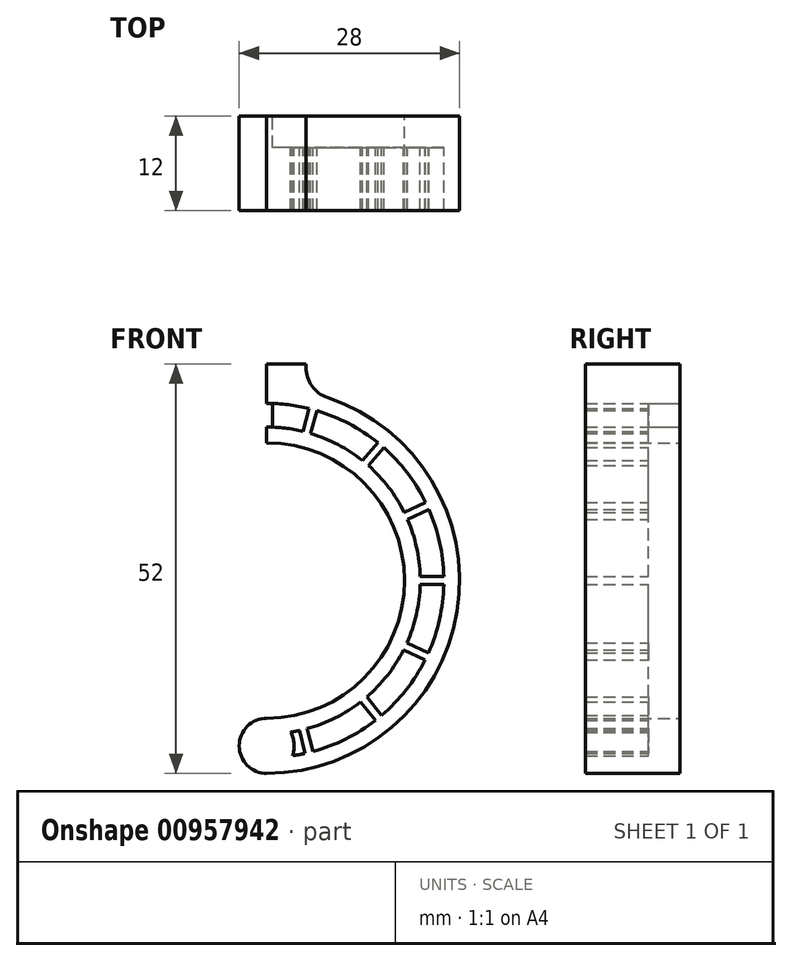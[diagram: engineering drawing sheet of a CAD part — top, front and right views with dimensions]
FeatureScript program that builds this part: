
annotation { "Feature Type Name" : "Feature", "Feature Type Description" : "" }
export const myFeature = defineFeature(function(context is Context, id is Id, definition is map)
    precondition{}
    {
        {
            var Q0;
            Q0=qCreatedBy(makeId("Front.planeOp"),FACE);
            var sketch = newSketch(context, id + "F0", { "sketchPlane" : qUnion([Q0])});
            skArc(sketch, "E0", {"start": v(0, -24.5) * mm, "mid": v(24.18, -3.92) * mm, "end": v(7.73, 23.25) * mm});
            skArc(sketch, "E1", {"start": v(0, -17.5) * mm, "mid": v(17.5, 0) * mm, "end": v(0, 17.5) * mm});
            skArc(sketch, "E2.0", {"start": v(3.04, -19.26) * mm, "mid": v(19.44, 1.52) * mm, "end": v(0, 19.5) * mm});
            skArc(sketch, "E3.0", {"start": v(3.26, -22.26) * mm, "mid": v(22.44, 1.64) * mm, "end": v(0, 22.5) * mm});
            skLineSegment(sketch, "E4", {"start": v(0, 0) * mm, "end": v(0, 29.22) * mm});
            skLineSegment(sketch, "E5", {"start": v(0, 29.22) * mm, "end": v(0, 0) * mm});
            skLineSegment(sketch, "E6", {"start": v(0, -27.59) * mm, "end": v(0, -24.5) * mm});
            skLineSegment(sketch, "E7.top", {"start": v(0, 27.5) * mm, "end": v(5, 27.5) * mm});
            skLineSegment(sketch, "E7.left", {"start": v(0, 17.5) * mm, "end": v(0, 27.5) * mm});
            skLineSegment(sketch, "E8.trimOffspring", {"start": v(5, 27.08) * mm, "end": v(5, 27.5) * mm});
            skCircle(sketch, "E9", {"center": v(0, -21) * mm, "radius": 3.5 * mm});
            skPoint(sketch, "E9.third.point", {"position": v(-3.48, -21.36) * mm});
            skLineSegment(sketch, "E10.trimOffspring", {"start": v(0, -17.5) * mm, "end": v(0, 0) * mm});
            skLineSegment(sketch, "E11.bottom", {"start": v(17.5, -0.5) * mm, "end": v(24.48, -0.5) * mm});
            skLineSegment(sketch, "E11.top", {"start": v(17.5, 0.5) * mm, "end": v(24.48, 0.5) * mm});
            skLineSegment(sketch, "E11.left", {"start": v(17.5, -0.5) * mm, "end": v(17.5, 0.5) * mm});
            skLineSegment(sketch, "E11.right", {"start": v(24.48, -0.5) * mm, "end": v(24.48, 0.5) * mm});
            skPoint(sketch, "E11.middle", {"position": v(20.99, 0) * mm});
            skLineSegment(sketch, "E12.1.0", {"start": v(15.59, -7.95) * mm, "end": v(16.02, -7.05) * mm});
            skLineSegment(sketch, "E12.1.1", {"start": v(21.9, -10.95) * mm, "end": v(22.33, -10.05) * mm});
            skLineSegment(sketch, "E12.1.2", {"start": v(15.59, -7.95) * mm, "end": v(21.9, -10.95) * mm});
            skLineSegment(sketch, "E12.1.3", {"start": v(16.02, -7.05) * mm, "end": v(22.33, -10.05) * mm});
            skLineSegment(sketch, "E12.2.0", {"start": v(10.67, -13.87) * mm, "end": v(11.45, -13.24) * mm});
            skLineSegment(sketch, "E12.2.1", {"start": v(15.1, -19.29) * mm, "end": v(15.87, -18.65) * mm});
            skLineSegment(sketch, "E12.2.2", {"start": v(10.67, -13.87) * mm, "end": v(15.1, -19.29) * mm});
            skLineSegment(sketch, "E12.2.3", {"start": v(11.45, -13.24) * mm, "end": v(15.87, -18.65) * mm});
            skLineSegment(sketch, "E12.3.0", {"start": v(3.7, -17.1) * mm, "end": v(4.66, -16.87) * mm});
            skLineSegment(sketch, "E12.3.1", {"start": v(5.36, -23.9) * mm, "end": v(6.33, -23.65) * mm});
            skLineSegment(sketch, "E12.3.2", {"start": v(3.7, -17.1) * mm, "end": v(5.36, -23.9) * mm});
            skLineSegment(sketch, "E12.3.3", {"start": v(4.66, -16.87) * mm, "end": v(6.33, -23.65) * mm});
            skLineSegment(sketch, "E12.anchor1", {"start": v(0, 0) * mm, "end": v(17.5, -0.5) * mm, "construction": true});
            skLineSegment(sketch, "E12.anchor2", {"start": v(0, 0) * mm, "end": v(3.7, -17.1) * mm, "construction": true});
            skLineSegment(sketch, "E13.1.0", {"start": v(16.07, 6.92) * mm, "end": v(15.65, 7.83) * mm});
            skLineSegment(sketch, "E13.1.1", {"start": v(22.4, 9.87) * mm, "end": v(21.99, 10.78) * mm});
            skLineSegment(sketch, "E13.1.2", {"start": v(16.07, 6.92) * mm, "end": v(22.4, 9.87) * mm});
            skLineSegment(sketch, "E13.1.3", {"start": v(15.65, 7.83) * mm, "end": v(21.99, 10.78) * mm});
            skLineSegment(sketch, "E13.2.0", {"start": v(11.65, 13.06) * mm, "end": v(10.89, 13.7) * mm});
            skLineSegment(sketch, "E13.2.1", {"start": v(16.15, 18.4) * mm, "end": v(15.4, 19.05) * mm});
            skLineSegment(sketch, "E13.2.2", {"start": v(11.65, 13.06) * mm, "end": v(16.15, 18.4) * mm});
            skLineSegment(sketch, "E13.2.3", {"start": v(10.89, 13.7) * mm, "end": v(15.4, 19.05) * mm});
            skLineSegment(sketch, "E13.anchor1", {"start": v(0, 0) * mm, "end": v(17.5, 0.5) * mm, "construction": true});
            skLineSegment(sketch, "E13.anchor2", {"start": v(0, 0) * mm, "end": v(4.1, 17.01) * mm, "construction": true});
            skLineSegment(sketch, "E14.2.3.0", {"start": v(5.06, 16.75) * mm, "end": v(4.1, 17.01) * mm});
            skLineSegment(sketch, "E14.6.3.0", {"start": v(5.06, 16.75) * mm, "end": v(6.37, 21.58) * mm});
            skLineSegment(sketch, "E14.9.3.0", {"start": v(4.1, 17.01) * mm, "end": v(5.4, 21.84) * mm});
            skArc(sketch, "E15.filletArc", {"start": v(5, 27.08) * mm, "mid": v(5.74, 24.72) * mm, "end": v(7.73, 23.25) * mm});
            skLineSegment(sketch, "E16.left", {"start": v(0, 22.5) * mm, "end": v(0, 19.5) * mm});
            skLineSegment(sketch, "E16.right", {"start": v(0.74, 22.49) * mm, "end": v(0.74, 19.49) * mm});
            skSolve(sketch);
        }
        {
            var Q0;
            {var subQ12=sQuery(id+"F0.wireOp",EDGE,"E0");Q0=makeQuery(id+"F0.imprint","IMPRINT",FACE,{"disambiguationData":[TD([[makeQuery(id+"F0.imprint","IMPRINT",EDGE,{"derivedFrom":subQ12}),1.0]])]});}
            var Q1;
            {var subQ5=sQuery(id+"F0.wireOp",EDGE,"E13.2.1");Q1=makeQuery(id+"F0.imprint","IMPRINT",FACE,{"disambiguationData":[TD([[makeQuery(id+"F0.imprint","IMPRINT",EDGE,{"derivedFrom":subQ5}),1.0]])]});}
            var Q2;
            {var subQ5=sQuery(id+"F0.wireOp",EDGE,"E13.1.1");Q2=makeQuery(id+"F0.imprint","IMPRINT",FACE,{"disambiguationData":[TD([[makeQuery(id+"F0.imprint","IMPRINT",EDGE,{"derivedFrom":subQ5}),1.0]])]});}
            var Q3;
            {var subQ5=sQuery(id+"F0.wireOp",EDGE,"E11.right");Q3=makeQuery(id+"F0.imprint","IMPRINT",FACE,{"disambiguationData":[TD([[makeQuery(id+"F0.imprint","IMPRINT",EDGE,{"derivedFrom":subQ5}),1.0]])]});}
            var Q4;
            {var subQ5=sQuery(id+"F0.wireOp",EDGE,"E12.1.1");Q4=makeQuery(id+"F0.imprint","IMPRINT",FACE,{"disambiguationData":[TD([[makeQuery(id+"F0.imprint","IMPRINT",EDGE,{"derivedFrom":subQ5}),1.0]])]});}
            var Q5;
            {var subQ5=sQuery(id+"F0.wireOp",EDGE,"E12.2.1");Q5=makeQuery(id+"F0.imprint","IMPRINT",FACE,{"disambiguationData":[TD([[makeQuery(id+"F0.imprint","IMPRINT",EDGE,{"derivedFrom":subQ5}),1.0]])]});}
            var Q6;
            {var subQ5=sQuery(id+"F0.wireOp",EDGE,"E12.3.1");Q6=makeQuery(id+"F0.imprint","IMPRINT",FACE,{"disambiguationData":[TD([[makeQuery(id+"F0.imprint","IMPRINT",EDGE,{"derivedFrom":subQ5}),1.0]])]});}
            var Q7;
            {var subQ3=sQuery(id+"F0.wireOp",EDGE,"E12.3.3");var subQ5=sQuery(id+"F0.wireOp",EDGE,"E2.0");var subQ6=makeQuery(id+"F0.imprint","INTERSECT",VERTEX,{"derivedFrom":[subQ5,subQ3]});Q7=makeQuery(id+"F0.imprint","IMPRINT",FACE,{"disambiguationData":[TD([[makeQuery(id+"F0.imprint","IMPRINT",EDGE,{"disambiguationData":[TD([[subQ6,-1.0]])],"derivedFrom":subQ5}),1.0]])]});}
            var Q8;
            {var subQ0=sQuery(id+"F0.wireOp",EDGE,"E12.3.2");var subQ6=sQuery(id+"F0.wireOp",EDGE,"E2.0");var subQ7=makeQuery(id+"F0.imprint","INTERSECT",VERTEX,{"derivedFrom":[subQ6,subQ0]});Q8=makeQuery(id+"F0.imprint","IMPRINT",FACE,{"disambiguationData":[TD([[makeQuery(id+"F0.imprint","IMPRINT",EDGE,{"disambiguationData":[TD([[subQ7,-1.0]])],"derivedFrom":subQ6}),1.0]])]});}
            var Q9;
            {var subQ0=sQuery(id+"F0.wireOp",EDGE,"E9");var subQ5=sQuery(id+"F0.wireOp",EDGE,"E2.0");var subQ6=makeQuery(id+"F0.imprint","INTERSECT",VERTEX,{"derivedFrom":[subQ5,subQ0]});Q9=makeQuery(id+"F0.imprint","IMPRINT",FACE,{"disambiguationData":[TD([[makeQuery(id+"F0.imprint","IMPRINT",EDGE,{"disambiguationData":[TD([[subQ6,-1.0]])],"derivedFrom":subQ5}),1.0]])]});}
            var Q10;
            {var subQ0=sQuery(id+"F0.wireOp",EDGE,"E9");var subQ3=makeQuery(id+"F0.imprint","INTERSECT",VERTEX,{"derivedFrom":[sQuery(id+"F0.wireOp",EDGE,"E0"),subQ0]});Q10=makeQuery(id+"F0.imprint","IMPRINT",FACE,{"disambiguationData":[TD([[makeQuery(id+"F0.imprint","IMPRINT",EDGE,{"disambiguationData":[TD([[subQ3,-1.0]])],"derivedFrom":subQ0}),1.0]])]});}
            var Q11;
            {var subQ0=sQuery(id+"F0.wireOp",EDGE,"E12.2.2");var subQ6=sQuery(id+"F0.wireOp",EDGE,"E2.0");var subQ7=makeQuery(id+"F0.imprint","INTERSECT",VERTEX,{"derivedFrom":[subQ6,subQ0]});Q11=makeQuery(id+"F0.imprint","IMPRINT",FACE,{"disambiguationData":[TD([[makeQuery(id+"F0.imprint","IMPRINT",EDGE,{"disambiguationData":[TD([[subQ7,-1.0]])],"derivedFrom":subQ6}),1.0]])]});}
            var Q12;
            {var subQ0=sQuery(id+"F0.wireOp",EDGE,"E12.3.2");var subQ1=sQuery(id+"F0.wireOp",EDGE,"E2.0");var subQ2=makeQuery(id+"F0.imprint","INTERSECT",VERTEX,{"derivedFrom":[subQ1,subQ0]});Q12=makeQuery(id+"F0.imprint","IMPRINT",FACE,{"disambiguationData":[TD([[makeQuery(id+"F0.imprint","IMPRINT",EDGE,{"disambiguationData":[TD([[subQ2,-1.0]])],"derivedFrom":subQ1}),-1.0]])]});}
            var Q13;
            {var subQ0=sQuery(id+"F0.wireOp",EDGE,"E12.2.2");var subQ1=sQuery(id+"F0.wireOp",EDGE,"E2.0");var subQ2=makeQuery(id+"F0.imprint","INTERSECT",VERTEX,{"derivedFrom":[subQ1,subQ0]});Q13=makeQuery(id+"F0.imprint","IMPRINT",FACE,{"disambiguationData":[TD([[makeQuery(id+"F0.imprint","IMPRINT",EDGE,{"disambiguationData":[TD([[subQ2,-1.0]])],"derivedFrom":subQ1}),-1.0]])]});}
            var Q14;
            {var subQ3=sQuery(id+"F0.wireOp",EDGE,"E12.2.3");var subQ5=sQuery(id+"F0.wireOp",EDGE,"E2.0");var subQ6=makeQuery(id+"F0.imprint","INTERSECT",VERTEX,{"derivedFrom":[subQ5,subQ3]});Q14=makeQuery(id+"F0.imprint","IMPRINT",FACE,{"disambiguationData":[TD([[makeQuery(id+"F0.imprint","IMPRINT",EDGE,{"disambiguationData":[TD([[subQ6,-1.0]])],"derivedFrom":subQ5}),1.0]])]});}
            var Q15;
            {var subQ0=sQuery(id+"F0.wireOp",EDGE,"E12.1.2");var subQ6=sQuery(id+"F0.wireOp",EDGE,"E2.0");var subQ7=makeQuery(id+"F0.imprint","INTERSECT",VERTEX,{"derivedFrom":[subQ6,subQ0]});Q15=makeQuery(id+"F0.imprint","IMPRINT",FACE,{"disambiguationData":[TD([[makeQuery(id+"F0.imprint","IMPRINT",EDGE,{"disambiguationData":[TD([[subQ7,-1.0]])],"derivedFrom":subQ6}),1.0]])]});}
            var Q16;
            {var subQ3=sQuery(id+"F0.wireOp",EDGE,"E12.1.3");var subQ5=sQuery(id+"F0.wireOp",EDGE,"E2.0");var subQ6=makeQuery(id+"F0.imprint","INTERSECT",VERTEX,{"derivedFrom":[subQ5,subQ3]});Q16=makeQuery(id+"F0.imprint","IMPRINT",FACE,{"disambiguationData":[TD([[makeQuery(id+"F0.imprint","IMPRINT",EDGE,{"disambiguationData":[TD([[subQ6,-1.0]])],"derivedFrom":subQ5}),1.0]])]});}
            var Q17;
            {var subQ1=sQuery(id+"F0.wireOp",EDGE,"E11.bottom");var subQ6=sQuery(id+"F0.wireOp",EDGE,"E2.0");var subQ7=makeQuery(id+"F0.imprint","INTERSECT",VERTEX,{"derivedFrom":[subQ6,subQ1]});Q17=makeQuery(id+"F0.imprint","IMPRINT",FACE,{"disambiguationData":[TD([[makeQuery(id+"F0.imprint","IMPRINT",EDGE,{"disambiguationData":[TD([[subQ7,-1.0]])],"derivedFrom":subQ6}),1.0]])]});}
            var Q18;
            {var subQ0=sQuery(id+"F0.wireOp",EDGE,"E11.top");var subQ5=sQuery(id+"F0.wireOp",EDGE,"E2.0");var subQ6=makeQuery(id+"F0.imprint","INTERSECT",VERTEX,{"derivedFrom":[subQ5,subQ0]});Q18=makeQuery(id+"F0.imprint","IMPRINT",FACE,{"disambiguationData":[TD([[makeQuery(id+"F0.imprint","IMPRINT",EDGE,{"disambiguationData":[TD([[subQ6,-1.0]])],"derivedFrom":subQ5}),1.0]])]});}
            var Q19;
            {var subQ0=sQuery(id+"F0.wireOp",EDGE,"E12.1.2");var subQ1=sQuery(id+"F0.wireOp",EDGE,"E2.0");var subQ2=makeQuery(id+"F0.imprint","INTERSECT",VERTEX,{"derivedFrom":[subQ1,subQ0]});Q19=makeQuery(id+"F0.imprint","IMPRINT",FACE,{"disambiguationData":[TD([[makeQuery(id+"F0.imprint","IMPRINT",EDGE,{"disambiguationData":[TD([[subQ2,-1.0]])],"derivedFrom":subQ1}),-1.0]])]});}
            var Q20;
            {var subQ0=sQuery(id+"F0.wireOp",EDGE,"E11.bottom");var subQ1=sQuery(id+"F0.wireOp",EDGE,"E2.0");var subQ2=makeQuery(id+"F0.imprint","INTERSECT",VERTEX,{"derivedFrom":[subQ1,subQ0]});Q20=makeQuery(id+"F0.imprint","IMPRINT",FACE,{"disambiguationData":[TD([[makeQuery(id+"F0.imprint","IMPRINT",EDGE,{"disambiguationData":[TD([[subQ2,-1.0]])],"derivedFrom":subQ1}),-1.0]])]});}
            var Q21;
            {var subQ0=sQuery(id+"F0.wireOp",EDGE,"E13.1.2");var subQ6=sQuery(id+"F0.wireOp",EDGE,"E2.0");var subQ7=makeQuery(id+"F0.imprint","INTERSECT",VERTEX,{"derivedFrom":[subQ6,subQ0]});Q21=makeQuery(id+"F0.imprint","IMPRINT",FACE,{"disambiguationData":[TD([[makeQuery(id+"F0.imprint","IMPRINT",EDGE,{"disambiguationData":[TD([[subQ7,-1.0]])],"derivedFrom":subQ6}),1.0]])]});}
            var Q22;
            {var subQ0=sQuery(id+"F0.wireOp",EDGE,"E13.1.2");var subQ1=sQuery(id+"F0.wireOp",EDGE,"E2.0");var subQ2=makeQuery(id+"F0.imprint","INTERSECT",VERTEX,{"derivedFrom":[subQ1,subQ0]});Q22=makeQuery(id+"F0.imprint","IMPRINT",FACE,{"disambiguationData":[TD([[makeQuery(id+"F0.imprint","IMPRINT",EDGE,{"disambiguationData":[TD([[subQ2,-1.0]])],"derivedFrom":subQ1}),-1.0]])]});}
            var Q23;
            {var subQ0=sQuery(id+"F0.wireOp",EDGE,"E13.1.3");var subQ5=sQuery(id+"F0.wireOp",EDGE,"E2.0");var subQ6=makeQuery(id+"F0.imprint","INTERSECT",VERTEX,{"derivedFrom":[subQ5,subQ0]});Q23=makeQuery(id+"F0.imprint","IMPRINT",FACE,{"disambiguationData":[TD([[makeQuery(id+"F0.imprint","IMPRINT",EDGE,{"disambiguationData":[TD([[subQ6,-1.0]])],"derivedFrom":subQ5}),1.0]])]});}
            var Q24;
            {var subQ0=sQuery(id+"F0.wireOp",EDGE,"E13.2.2");var subQ6=sQuery(id+"F0.wireOp",EDGE,"E2.0");var subQ7=makeQuery(id+"F0.imprint","INTERSECT",VERTEX,{"derivedFrom":[subQ6,subQ0]});Q24=makeQuery(id+"F0.imprint","IMPRINT",FACE,{"disambiguationData":[TD([[makeQuery(id+"F0.imprint","IMPRINT",EDGE,{"disambiguationData":[TD([[subQ7,-1.0]])],"derivedFrom":subQ6}),1.0]])]});}
            var Q25;
            {var subQ0=sQuery(id+"F0.wireOp",EDGE,"E13.2.2");var subQ1=sQuery(id+"F0.wireOp",EDGE,"E2.0");var subQ2=makeQuery(id+"F0.imprint","INTERSECT",VERTEX,{"derivedFrom":[subQ1,subQ0]});Q25=makeQuery(id+"F0.imprint","IMPRINT",FACE,{"disambiguationData":[TD([[makeQuery(id+"F0.imprint","IMPRINT",EDGE,{"disambiguationData":[TD([[subQ2,-1.0]])],"derivedFrom":subQ1}),-1.0]])]});}
            var Q26;
            {var subQ0=sQuery(id+"F0.wireOp",EDGE,"E13.2.3");var subQ5=sQuery(id+"F0.wireOp",EDGE,"E2.0");var subQ6=makeQuery(id+"F0.imprint","INTERSECT",VERTEX,{"derivedFrom":[subQ5,subQ0]});Q26=makeQuery(id+"F0.imprint","IMPRINT",FACE,{"disambiguationData":[TD([[makeQuery(id+"F0.imprint","IMPRINT",EDGE,{"disambiguationData":[TD([[subQ6,-1.0]])],"derivedFrom":subQ5}),1.0]])]});}
            var Q27;
            {var subQ0=sQuery(id+"F0.wireOp",EDGE,"E14.6.3.0");var subQ1=sQuery(id+"F0.wireOp",EDGE,"E2.0");var subQ2=makeQuery(id+"F0.imprint","INTERSECT",VERTEX,{"derivedFrom":[subQ1,subQ0]});Q27=makeQuery(id+"F0.imprint","IMPRINT",FACE,{"disambiguationData":[TD([[makeQuery(id+"F0.imprint","IMPRINT",EDGE,{"disambiguationData":[TD([[subQ2,-1.0]])],"derivedFrom":subQ1}),-1.0]])]});}
            var Q28;
            {var subQ0=sQuery(id+"F0.wireOp",EDGE,"E14.6.3.0");var subQ6=sQuery(id+"F0.wireOp",EDGE,"E2.0");var subQ7=makeQuery(id+"F0.imprint","INTERSECT",VERTEX,{"derivedFrom":[subQ6,subQ0]});Q28=makeQuery(id+"F0.imprint","IMPRINT",FACE,{"disambiguationData":[TD([[makeQuery(id+"F0.imprint","IMPRINT",EDGE,{"disambiguationData":[TD([[subQ7,-1.0]])],"derivedFrom":subQ6}),1.0]])]});}
            var Q29;
            {var subQ0=sQuery(id+"F0.wireOp",EDGE,"E7.left");var subQ5=sQuery(id+"F0.wireOp",EDGE,"E2.0");var subQ6=makeQuery(id+"F0.imprint","INTERSECT",VERTEX,{"derivedFrom":[subQ5,subQ0]});Q29=makeQuery(id+"F0.imprint","IMPRINT",FACE,{"disambiguationData":[TD([[makeQuery(id+"F0.imprint","IMPRINT",EDGE,{"disambiguationData":[TD([[subQ6,1.0]])],"derivedFrom":subQ5}),1.0]])]});}
            var Q30;
            {var subQ0=sQuery(id+"F0.wireOp",EDGE,"E16.left");Q30=makeQuery(id+"F0.imprint","IMPRINT",FACE,{"disambiguationData":[TD([[makeQuery(id+"F0.imprint","IMPRINT",EDGE,{"derivedFrom":subQ0}),1.0]])]});}
            extrude(context, id + "F1", {"entities" : qUnion([Q0, Q1, Q2, Q3, Q4, Q5, Q6, Q7, Q8, Q9, Q10, Q11, Q12, Q13, Q14, Q15, Q16, Q17, Q18, Q19, Q20, Q21, Q22, Q23, Q24, Q25, Q26, Q27, Q28, Q29, Q30]), "depth" : 12 * mm, "offsetDistance" : 25 * mm});
        }
        {
            var Q0;
            {var subQ0=sQuery(id+"F0.wireOp",EDGE,"E12.3.3");var subQ1=sQuery(id+"F0.wireOp",EDGE,"E2.0");var subQ2=makeQuery(id+"F0.imprint","INTERSECT",VERTEX,{"derivedFrom":[subQ1,subQ0]});Q0=makeQuery(id+"F0.imprint","IMPRINT",FACE,{"disambiguationData":[TD([[makeQuery(id+"F0.imprint","IMPRINT",EDGE,{"disambiguationData":[TD([[subQ2,-1.0]])],"derivedFrom":subQ1}),-1.0]])]});}
            var Q1;
            {var subQ0=sQuery(id+"F0.wireOp",EDGE,"E11.top");var subQ1=sQuery(id+"F0.wireOp",EDGE,"E2.0");var subQ2=makeQuery(id+"F0.imprint","INTERSECT",VERTEX,{"derivedFrom":[subQ1,subQ0]});Q1=makeQuery(id+"F0.imprint","IMPRINT",FACE,{"disambiguationData":[TD([[makeQuery(id+"F0.imprint","IMPRINT",EDGE,{"disambiguationData":[TD([[subQ2,-1.0]])],"derivedFrom":subQ1}),-1.0]])]});}
            var Q2;
            {var subQ0=sQuery(id+"F0.wireOp",EDGE,"E13.1.3");var subQ1=sQuery(id+"F0.wireOp",EDGE,"E2.0");var subQ2=makeQuery(id+"F0.imprint","INTERSECT",VERTEX,{"derivedFrom":[subQ1,subQ0]});Q2=makeQuery(id+"F0.imprint","IMPRINT",FACE,{"disambiguationData":[TD([[makeQuery(id+"F0.imprint","IMPRINT",EDGE,{"disambiguationData":[TD([[subQ2,-1.0]])],"derivedFrom":subQ1}),-1.0]])]});}
            var Q3;
            {var subQ0=sQuery(id+"F0.wireOp",EDGE,"E12.1.3");var subQ1=sQuery(id+"F0.wireOp",EDGE,"E2.0");var subQ2=makeQuery(id+"F0.imprint","INTERSECT",VERTEX,{"derivedFrom":[subQ1,subQ0]});Q3=makeQuery(id+"F0.imprint","IMPRINT",FACE,{"disambiguationData":[TD([[makeQuery(id+"F0.imprint","IMPRINT",EDGE,{"disambiguationData":[TD([[subQ2,-1.0]])],"derivedFrom":subQ1}),-1.0]])]});}
            var Q4;
            {var subQ0=sQuery(id+"F0.wireOp",EDGE,"E13.2.3");var subQ1=sQuery(id+"F0.wireOp",EDGE,"E2.0");var subQ2=makeQuery(id+"F0.imprint","INTERSECT",VERTEX,{"derivedFrom":[subQ1,subQ0]});Q4=makeQuery(id+"F0.imprint","IMPRINT",FACE,{"disambiguationData":[TD([[makeQuery(id+"F0.imprint","IMPRINT",EDGE,{"disambiguationData":[TD([[subQ2,-1.0]])],"derivedFrom":subQ1}),-1.0]])]});}
            var Q5;
            {var subQ0=sQuery(id+"F0.wireOp",EDGE,"E9");var subQ1=sQuery(id+"F0.wireOp",EDGE,"E2.0");var subQ2=makeQuery(id+"F0.imprint","INTERSECT",VERTEX,{"derivedFrom":[subQ1,subQ0]});Q5=makeQuery(id+"F0.imprint","IMPRINT",FACE,{"disambiguationData":[TD([[makeQuery(id+"F0.imprint","IMPRINT",EDGE,{"disambiguationData":[TD([[subQ2,-1.0]])],"derivedFrom":subQ1}),-1.0]])]});}
            var Q6;
            {var subQ0=sQuery(id+"F0.wireOp",EDGE,"E12.2.3");var subQ1=sQuery(id+"F0.wireOp",EDGE,"E2.0");var subQ2=makeQuery(id+"F0.imprint","INTERSECT",VERTEX,{"derivedFrom":[subQ1,subQ0]});Q6=makeQuery(id+"F0.imprint","IMPRINT",FACE,{"disambiguationData":[TD([[makeQuery(id+"F0.imprint","IMPRINT",EDGE,{"disambiguationData":[TD([[subQ2,-1.0]])],"derivedFrom":subQ1}),-1.0]])]});}
            var Q7;
            {var subQ0=sQuery(id+"F0.wireOp",EDGE,"E16.right");Q7=makeQuery(id+"F0.imprint","IMPRINT",FACE,{"disambiguationData":[TD([[makeQuery(id+"F0.imprint","IMPRINT",EDGE,{"derivedFrom":subQ0}),1.0]])]});}
            extrude(context, id + "F2", {"entities" : qUnion([Q0, Q1, Q2, Q3, Q4, Q5, Q6, Q7]), "operationType" : NewBodyOperationType.ADD, "depth" : 4 * mm, "offsetDistance" : 25 * mm});
        }
    });
